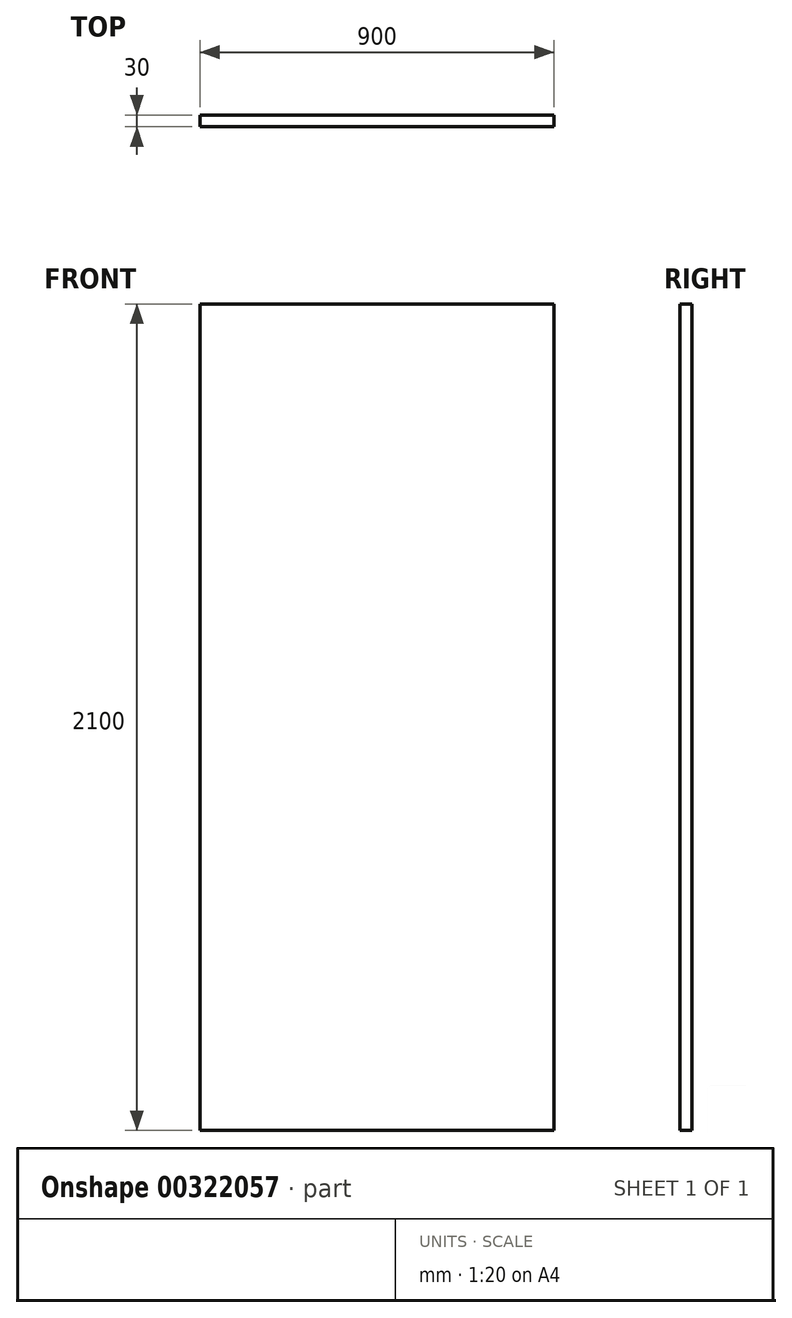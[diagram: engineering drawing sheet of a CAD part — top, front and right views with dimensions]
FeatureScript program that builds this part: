
annotation { "Feature Type Name" : "Feature", "Feature Type Description" : "" }
export const myFeature = defineFeature(function(context is Context, id is Id, definition is map)
    precondition{}
    {
        {
            var Q0;
            Q0=qCreatedBy(makeId("Front.planeOp"),FACE);
            var sketch = newSketch(context, id + "F0", { "sketchPlane" : qUnion([Q0])});
            skLineSegment(sketch, "E0.bottom", {"start": v(450, 1050) * mm, "end": v(-450, 1050) * mm});
            skLineSegment(sketch, "E0.top", {"start": v(450, -1050) * mm, "end": v(-450, -1050) * mm});
            skLineSegment(sketch, "E0.left", {"start": v(450, 1050) * mm, "end": v(450, -1050) * mm});
            skLineSegment(sketch, "E0.right", {"start": v(-450, 1050) * mm, "end": v(-450, -1050) * mm});
            skPoint(sketch, "E0.middle", {"position": v(0, 0) * mm});
            skSolve(sketch);
        }
        {
            var Q0;
            Q0=makeQuery(id+"F0.imprint","IMPRINT",FACE,{"disambiguationData":[TD([[makeQuery(id+"F0.imprint","IMPRINT",EDGE,{"derivedFrom":sQuery(id+"F0.wireOp",EDGE,"E0.bottom")}),1.0]])]});
            extrude(context, id + "F1", {"entities" : qUnion([Q0]), "depth" : 30 * mm});
        }
    });
